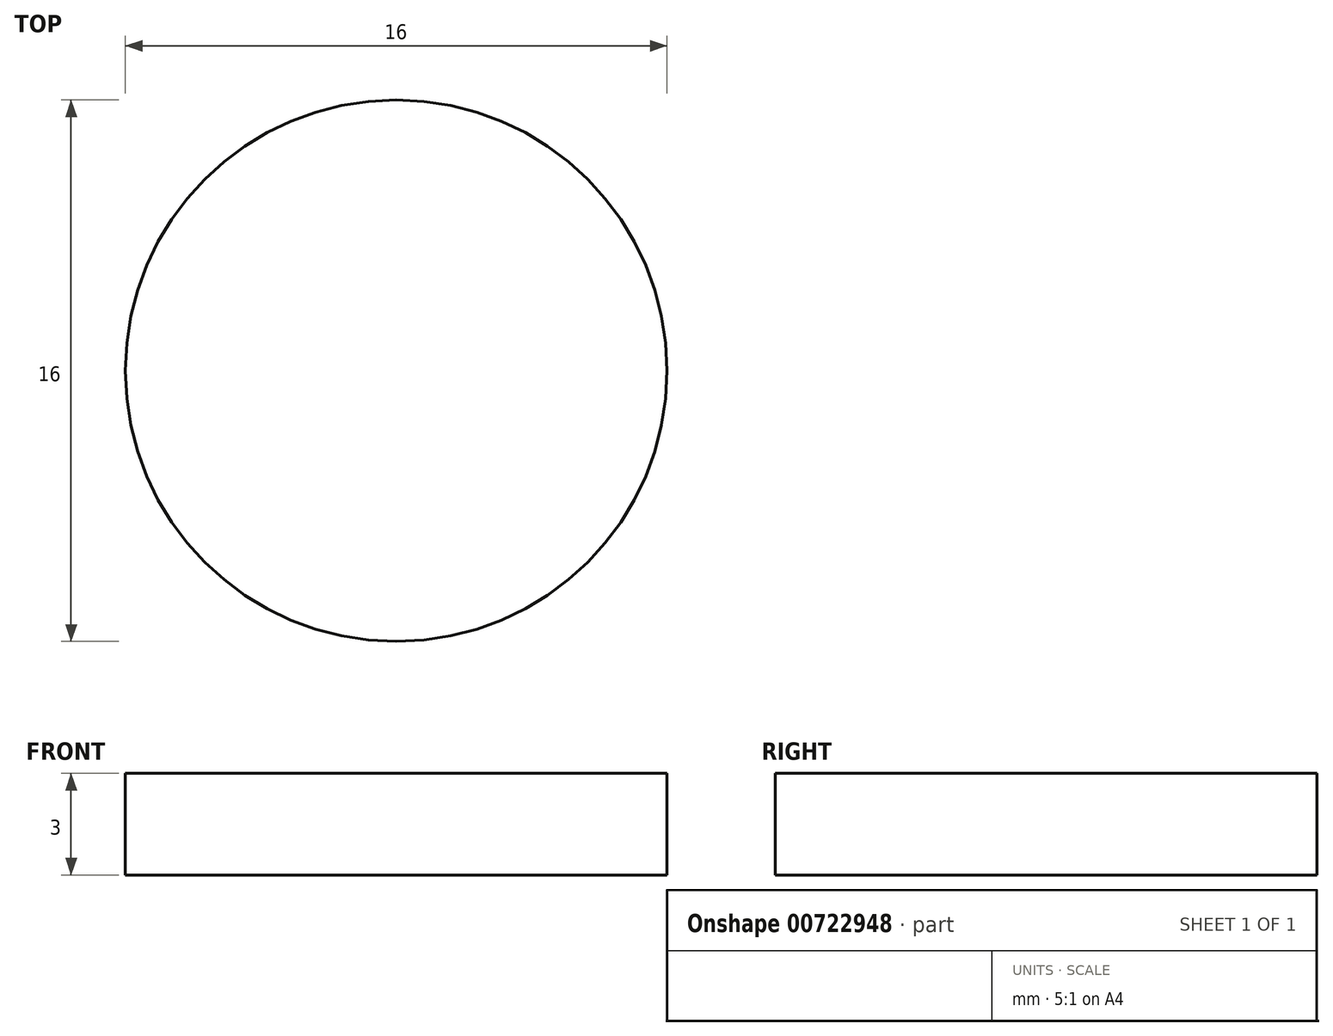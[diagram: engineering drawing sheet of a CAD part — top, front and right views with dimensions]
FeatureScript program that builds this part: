
annotation { "Feature Type Name" : "Feature", "Feature Type Description" : "" }
export const myFeature = defineFeature(function(context is Context, id is Id, definition is map)
    precondition{}
    {
        {
            var Q0;
            Q0=qCreatedBy(makeId("Top.planeOp"),FACE);
            var sketch = newSketch(context, id + "F0", { "sketchPlane" : qUnion([Q0])});
            skCircle(sketch, "E0", {"center": v(0, 0) * mm, "radius": 8 * mm});
            skSolve(sketch);
        }
        {
            var Q0;
            Q0 = qSketchRegion(id + "F0", true);
            extrude(context, id + "F1", {"entities" : qUnion([Q0]), "depth" : 3 * mm, "offsetDistance" : 25 * mm});
        }
    });
